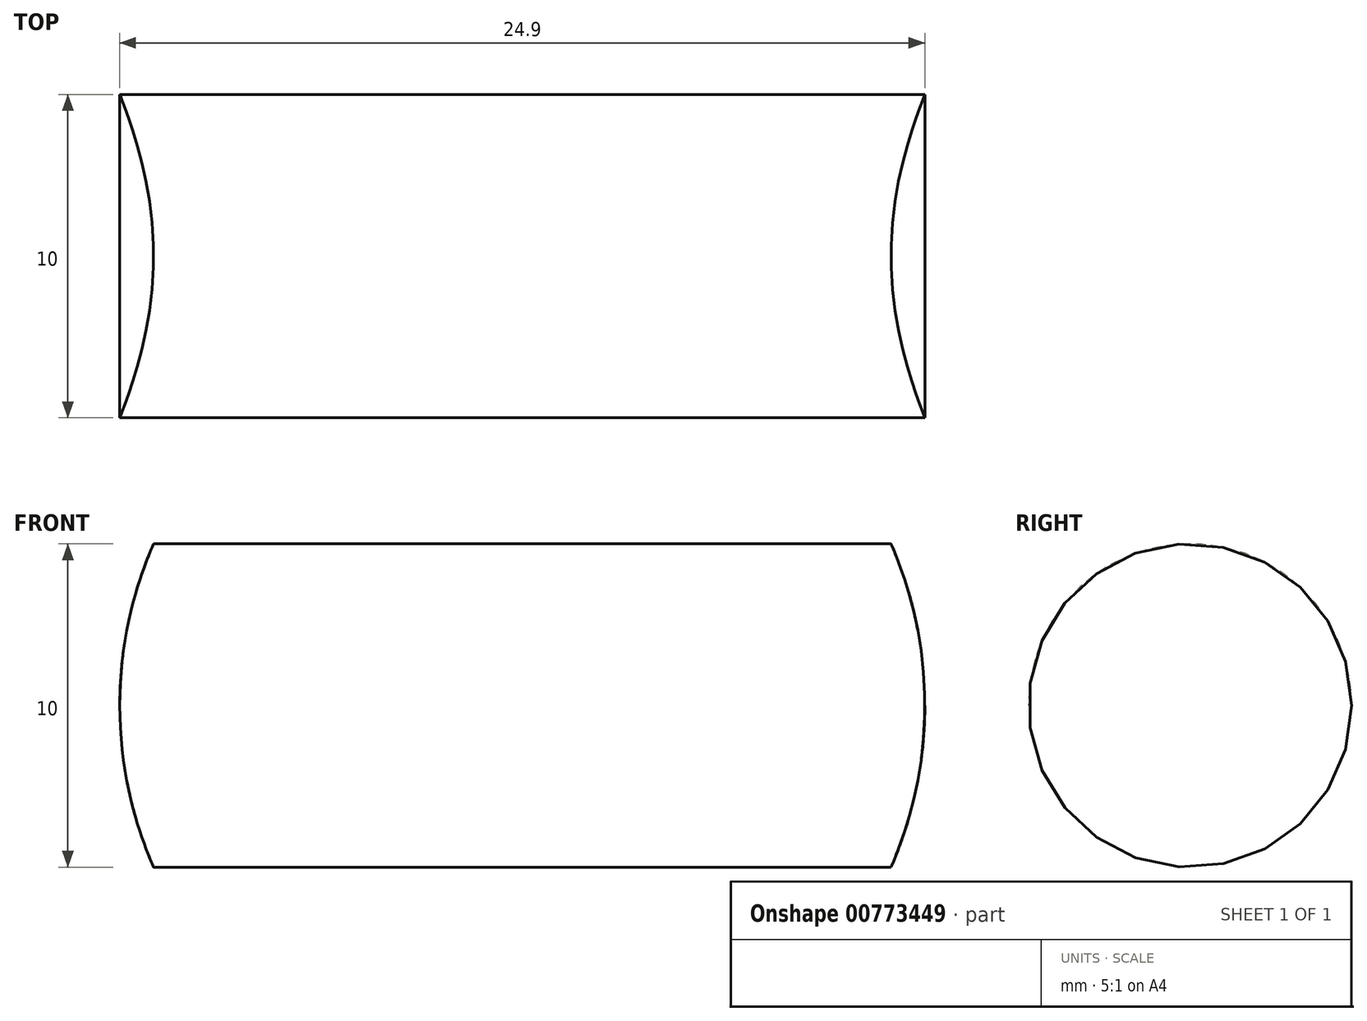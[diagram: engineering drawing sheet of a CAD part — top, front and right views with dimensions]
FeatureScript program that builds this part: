
annotation { "Feature Type Name" : "Feature", "Feature Type Description" : "" }
export const myFeature = defineFeature(function(context is Context, id is Id, definition is map)
    precondition{}
    {
        {
            var Q0;
            Q0=qCreatedBy(makeId("Front.planeOp"),FACE);
            var sketch = newSketch(context, id + "F0", { "sketchPlane" : qUnion([Q0])});
            skLineSegment(sketch, "E0.bottom", {"start": v(-12.45, 5) * mm, "end": v(12.45, 5) * mm});
            skLineSegment(sketch, "E0.top", {"start": v(-12.45, -5) * mm, "end": v(12.45, -5) * mm});
            skLineSegment(sketch, "E0.left", {"start": v(-12.45, 5) * mm, "end": v(-12.45, -5) * mm});
            skLineSegment(sketch, "E0.right", {"start": v(12.45, 5) * mm, "end": v(12.45, -5) * mm});
            skPoint(sketch, "E0.middle", {"position": v(0, 0) * mm});
            skSolve(sketch);
        }
        {
            var Q0;
            Q0 = qSketchRegion(id + "F0", true);
            extrude(context, id + "F1", {"entities" : qUnion([Q0]), "depth" : 10 * mm, "offsetDistance" : 25 * mm});
        }
        {
            var Q0;
            Q0=makeQuery(id+"F1.opExtrude","CAP_FACE",FACE,{"disambiguationData":[OSD([sQuery(id+"F0.wireOp",EDGE,"E0.bottom"),sQuery(id+"F0.wireOp",EDGE,"E0.top"),sQuery(id+"F0.wireOp",EDGE,"E0.left"),sQuery(id+"F0.wireOp",EDGE,"E0.right")])],"isStart":false});
            var sketch = newSketch(context, id + "F2", { "sketchPlane" : qUnion([Q0])});
            skCircle(sketch, "E1", {"center": v(0, 0) * mm, "radius": 12.45 * mm});
            skSolve(sketch);
        }
        {
            var Q0;
            Q0=makeQuery(id+"F1.opExtrude","SWEPT_FACE",FACE,{"disambiguationData":[OSD([sQuery(id+"F0.wireOp",EDGE,"E0.left")])]});
            var sketch = newSketch(context, id + "F3", { "sketchPlane" : qUnion([Q0])});
            skPoint(sketch, "E2", {"position": v(5, 0) * mm});
            skCircle(sketch, "E3", {"center": v(5, 0) * mm, "radius": 5 * mm});
            skSolve(sketch);
        }
        {
            var Q0;
            {var subQ0=sQuery(id+"F3.wireOp",EDGE,"E3");var subQ1=sQuery(id+"F0.wireOp",EDGE,"E0.left");var subQ4=makeQuery(id+"F1.opExtrude","CAP_EDGE",EDGE,{"disambiguationData":[OSD([subQ1])],"isStart":true});var subQ5=makeQuery(id+"F3.imprint","INTERSECT",VERTEX,{"derivedFrom":[subQ4,subQ0]});Q0=makeQuery(id+"F3.imprint","IMPRINT",FACE,{"disambiguationData":[TD([[makeQuery(id+"F3.imprint","IMPRINT",EDGE,{"disambiguationData":[TD([[subQ5,1.0]])],"derivedFrom":subQ0}),-1.0]])]});}
            var Q1;
            {var subQ0=sQuery(id+"F3.wireOp",EDGE,"E3");var subQ1=sQuery(id+"F0.wireOp",EDGE,"E0.left");var subQ4=makeQuery(id+"F1.opExtrude","CAP_EDGE",EDGE,{"disambiguationData":[OSD([subQ1])],"isStart":false});var subQ5=makeQuery(id+"F3.imprint","INTERSECT",VERTEX,{"derivedFrom":[subQ4,subQ0]});Q1=makeQuery(id+"F3.imprint","IMPRINT",FACE,{"disambiguationData":[TD([[makeQuery(id+"F3.imprint","IMPRINT",EDGE,{"disambiguationData":[TD([[subQ5,-1.0]])],"derivedFrom":subQ0}),-1.0]])]});}
            var Q2;
            {var subQ0=sQuery(id+"F3.wireOp",EDGE,"E3");var subQ1=sQuery(id+"F0.wireOp",EDGE,"E0.left");var subQ2=makeQuery(id+"F1.opExtrude","CAP_EDGE",EDGE,{"disambiguationData":[OSD([subQ1])],"isStart":true});var subQ3=makeQuery(id+"F3.imprint","INTERSECT",VERTEX,{"derivedFrom":[subQ2,subQ0]});Q2=makeQuery(id+"F3.imprint","IMPRINT",FACE,{"disambiguationData":[TD([[makeQuery(id+"F3.imprint","IMPRINT",EDGE,{"disambiguationData":[TD([[subQ3,-1.0]])],"derivedFrom":subQ0}),-1.0]])]});}
            var Q3;
            {var subQ0=sQuery(id+"F3.wireOp",EDGE,"E3");var subQ1=sQuery(id+"F0.wireOp",EDGE,"E0.left");var subQ2=makeQuery(id+"F1.opExtrude","CAP_EDGE",EDGE,{"disambiguationData":[OSD([subQ1])],"isStart":false});var subQ3=makeQuery(id+"F3.imprint","INTERSECT",VERTEX,{"derivedFrom":[subQ2,subQ0]});Q3=makeQuery(id+"F3.imprint","IMPRINT",FACE,{"disambiguationData":[TD([[makeQuery(id+"F3.imprint","IMPRINT",EDGE,{"disambiguationData":[TD([[subQ3,1.0]])],"derivedFrom":subQ0}),-1.0]])]});}
            extrude(context, id + "F4", {"entities" : qUnion([Q0, Q1, Q2, Q3]), "operationType" : NewBodyOperationType.REMOVE, "endBound" : BoundingType.THROUGH_ALL, "oppositeDirection" : true, "depth" : 25 * mm, "offsetDistance" : 25 * mm});
        }
        {
            var Q0;
            {var subQ0=sQuery(id+"F2.wireOp",EDGE,"E1");var subQ1=makeQuery(id+"F1.opExtrude","CAP_EDGE",EDGE,{"disambiguationData":[OSD([sQuery(id+"F0.wireOp",EDGE,"E0.bottom")])],"isStart":false});var subQ2=makeQuery(id+"F2.imprint","INTERSECT",VERTEX,{"disambiguationData":[OD(1.0)],"derivedFrom":[subQ1,subQ0]});Q0=makeQuery(id+"F2.imprint","IMPRINT",FACE,{"disambiguationData":[TD([[makeQuery(id+"F2.imprint","IMPRINT",EDGE,{"disambiguationData":[TD([[subQ2,-1.0]])],"derivedFrom":subQ0}),-1.0]])]});}
            var Q1;
            {var subQ0=sQuery(id+"F2.wireOp",EDGE,"E1");var subQ1=makeQuery(id+"F1.opExtrude","CAP_EDGE",EDGE,{"disambiguationData":[OSD([sQuery(id+"F0.wireOp",EDGE,"E0.left")])],"isStart":false});var subQ2=makeQuery(id+"F2.imprint","INTERSECT",VERTEX,{"derivedFrom":[subQ1,subQ0]});Q1=makeQuery(id+"F2.imprint","IMPRINT",FACE,{"disambiguationData":[TD([[makeQuery(id+"F2.imprint","IMPRINT",EDGE,{"disambiguationData":[TD([[subQ2,-1.0]])],"derivedFrom":subQ0}),-1.0]])]});}
            var Q2;
            {var subQ0=sQuery(id+"F2.wireOp",EDGE,"E1");var subQ1=makeQuery(id+"F1.opExtrude","CAP_EDGE",EDGE,{"disambiguationData":[OSD([sQuery(id+"F0.wireOp",EDGE,"E0.bottom")])],"isStart":false});var subQ2=makeQuery(id+"F2.imprint","INTERSECT",VERTEX,{"disambiguationData":[OD(0.0)],"derivedFrom":[subQ1,subQ0]});Q2=makeQuery(id+"F2.imprint","IMPRINT",FACE,{"disambiguationData":[TD([[makeQuery(id+"F2.imprint","IMPRINT",EDGE,{"disambiguationData":[TD([[subQ2,1.0]])],"derivedFrom":subQ0}),-1.0]])]});}
            var Q3;
            {var subQ0=sQuery(id+"F2.wireOp",EDGE,"E1");var subQ1=makeQuery(id+"F1.opExtrude","CAP_EDGE",EDGE,{"disambiguationData":[OSD([sQuery(id+"F0.wireOp",EDGE,"E0.right")])],"isStart":false});var subQ2=makeQuery(id+"F2.imprint","INTERSECT",VERTEX,{"derivedFrom":[subQ1,subQ0]});Q3=makeQuery(id+"F2.imprint","IMPRINT",FACE,{"disambiguationData":[TD([[makeQuery(id+"F2.imprint","IMPRINT",EDGE,{"disambiguationData":[TD([[subQ2,1.0]])],"derivedFrom":subQ0}),-1.0]])]});}
            extrude(context, id + "F5", {"entities" : qUnion([Q0, Q1, Q2, Q3]), "operationType" : NewBodyOperationType.REMOVE, "endBound" : BoundingType.THROUGH_ALL, "oppositeDirection" : true, "depth" : 25 * mm, "offsetDistance" : 25 * mm});
        }
    });
